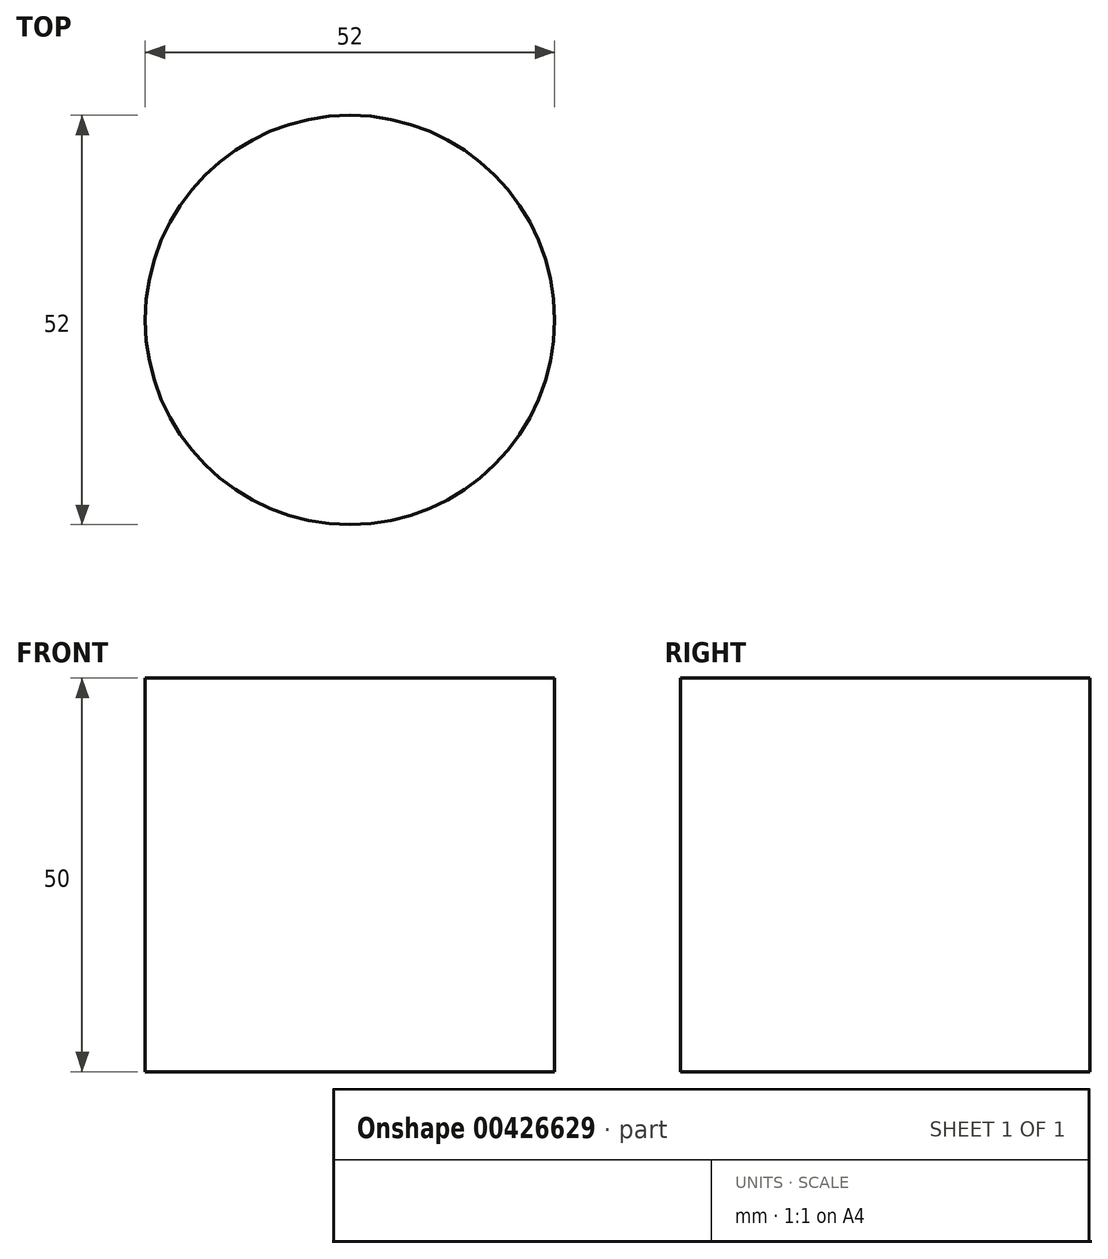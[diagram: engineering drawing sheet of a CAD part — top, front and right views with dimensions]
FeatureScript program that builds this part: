
annotation { "Feature Type Name" : "Feature", "Feature Type Description" : "" }
export const myFeature = defineFeature(function(context is Context, id is Id, definition is map)
    precondition{}
    {
        {
            var Q0;
            Q0=qCreatedBy(makeId("Top.planeOp"),FACE);
            var sketch = newSketch(context, id + "F0", { "sketchPlane" : qUnion([Q0])});
            skCircle(sketch, "E0", {"center": v(0, 0) * mm, "radius": 26 * mm});
            skSolve(sketch);
        }
        {
            var Q0;
            Q0 = qSketchRegion(id + "F0", true);
            extrude(context, id + "F1", {"entities" : qUnion([Q0]), "depth" : 50 * mm});
        }
        {
            var Q0;
            Q0=makeQuery(id+"F1.opExtrude","CAP_FACE",FACE,{"disambiguationData":[OSD([sQuery(id+"F0.wireOp",EDGE,"E0")])],"isStart":false});
            var sketch = newSketch(context, id + "F2", { "sketchPlane" : qUnion([Q0])});
            skCircle(sketch, "E1", {"center": v(0, 0) * mm, "radius": 37.5 * mm});
            skSolve(sketch);
        }
        {
            var Q0;
            Q0=makeQuery(id+"F2.imprint","IMPRINT",FACE,{"disambiguationData":[TD([[makeQuery(id+"F2.imprint","IMPRINT",EDGE,{"derivedFrom":sQuery(id+"F2.wireOp",EDGE,"E1")}),1.0]])]});
            extrude(context, id + "F3", {"entities" : qUnion([Q0]), "operationType" : NewBodyOperationType.REMOVE, "depth" : 25 * mm});
        }
    });
